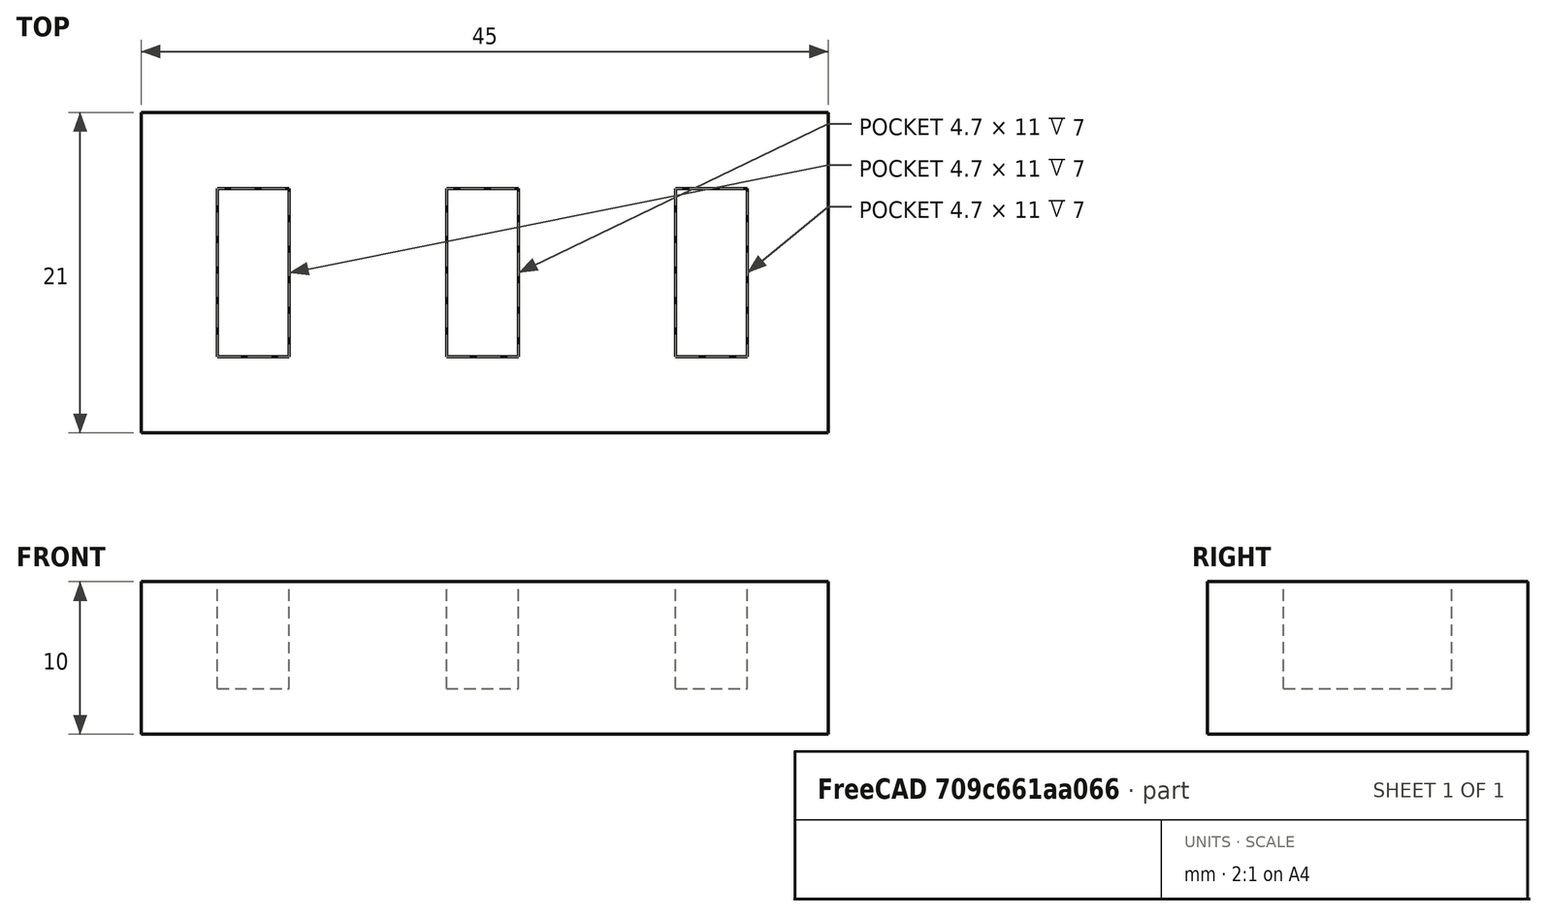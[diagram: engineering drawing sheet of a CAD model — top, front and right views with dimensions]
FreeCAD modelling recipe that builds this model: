
FCSTD DOCUMENT  (FreeCAD 0.16R6706 (Git))
Label: Ejercicos de la primera semana
License: All rights reserved
LicenseURL: http://en.wikipedia.org/wiki/All_rights_reserved
objects: Part::Box×4, Part::Cut×3
note: 7 computed .brp shape members not serialized (recipe doc carries the construction recipe); baked Part::Feature solids carry a one-line shape summary decoded from their .brp

FEATURE [Part::Box] Box  label="Cubo"
  Height = 10
  Length = 45
  Width = 21
FEATURE [Part::Box] Box001  label="Hueco"
  Height = 9
  Length = 4.7
  Placement = pos=(5,5,3) rot=(0,0,1;0rad)
  Width = 11
FEATURE [Part::Box] Box002  label="Hueco001"
  Height = 9
  Length = 4.7
  Placement = pos=(20,5,3) rot=(0,0,1;0rad)
  Width = 11
FEATURE [Part::Box] Box003  label="Hueco002"
  Height = 9
  Length = 4.7
  Placement = pos=(35,5,3) rot=(0,0,1;0rad)
  Width = 11
FEATURE [Part::Cut] Cut
  Base = -> Box
  Tool = -> Box001
FEATURE [Part::Cut] Cut001
  Base = -> Cut
  Tool = -> Box003
FEATURE [Part::Cut] Cut002
  Base = -> Cut001
  Tool = -> Box002
